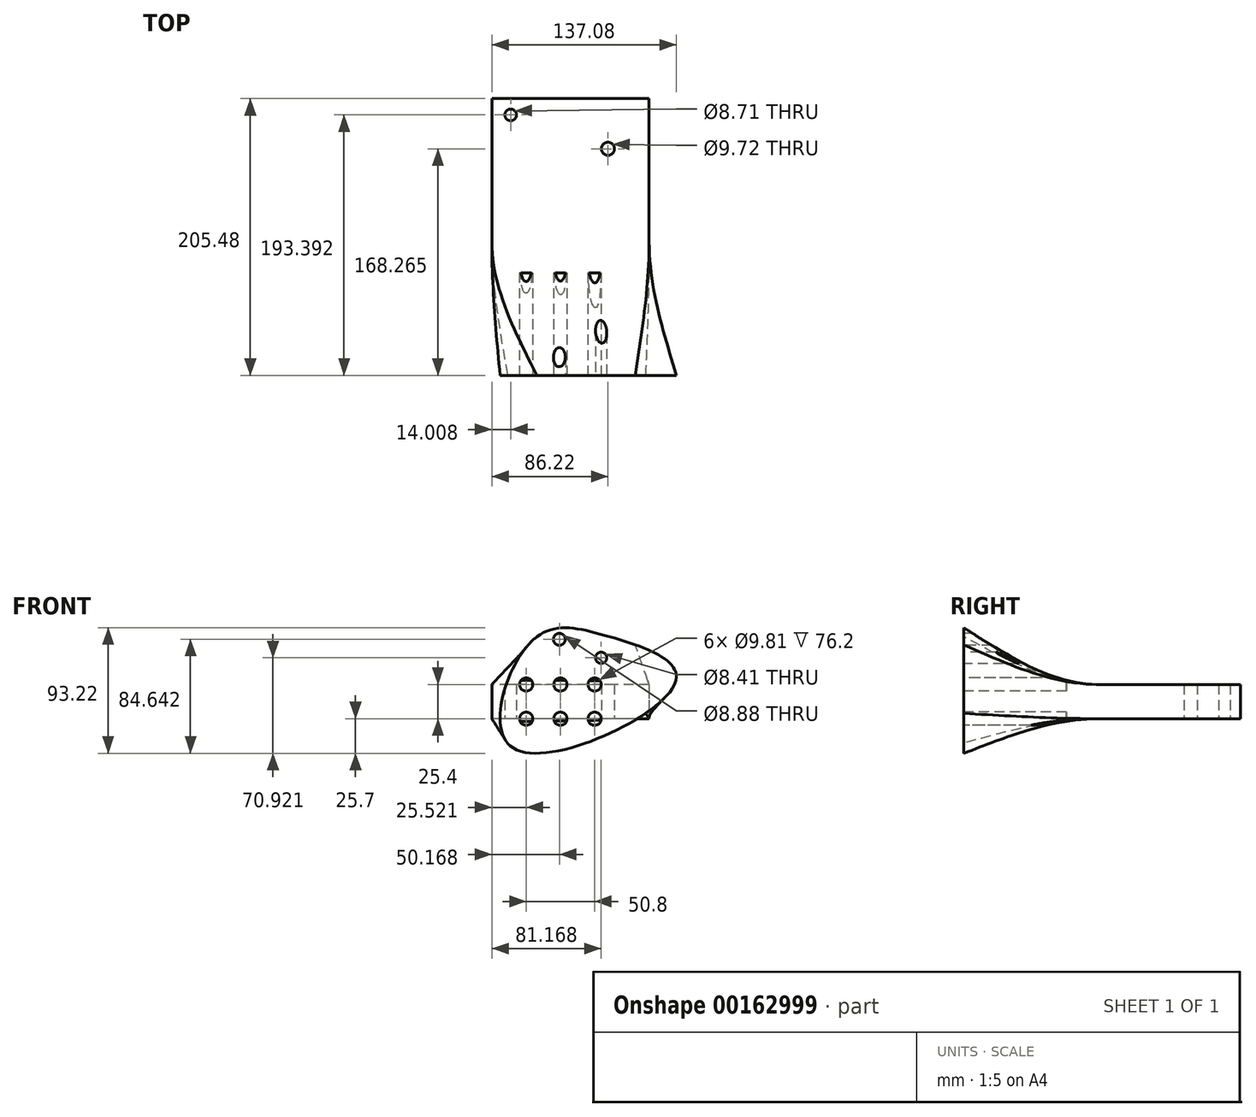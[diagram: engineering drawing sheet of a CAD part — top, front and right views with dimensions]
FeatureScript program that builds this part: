
annotation { "Feature Type Name" : "Feature", "Feature Type Description" : "" }
export const myFeature = defineFeature(function(context is Context, id is Id, definition is map)
    precondition{}
    {
        {
            var Q0;
            Q0=qCreatedBy(makeId("Top.planeOp"),FACE);
            var sketch = newSketch(context, id + "F0", { "sketchPlane" : qUnion([Q0])});
            skLineSegment(sketch, "E0.bottom", {"start": v(58.4, 53.08) * mm, "end": v(-58.4, 53.08) * mm});
            skLineSegment(sketch, "E0.top", {"start": v(58.4, -53.08) * mm, "end": v(-58.4, -53.08) * mm});
            skLineSegment(sketch, "E0.left", {"start": v(58.4, 53.08) * mm, "end": v(58.4, -53.08) * mm});
            skLineSegment(sketch, "E0.right", {"start": v(-58.4, 53.08) * mm, "end": v(-58.4, -53.08) * mm});
            skPoint(sketch, "E0.middle", {"position": v(0, 0) * mm});
            skCircle(sketch, "E1", {"center": v(-44.4, 41) * mm, "radius": 4.35 * mm});
            skCircle(sketch, "E2", {"center": v(27.82, 15.87) * mm, "radius": 4.86 * mm});
            skSolve(sketch);
        }
        {
            var Q0;
            Q0=makeQuery(id+"F0.imprint","IMPRINT",FACE,{"disambiguationData":[TD([[makeQuery(id+"F0.imprint","IMPRINT",EDGE,{"derivedFrom":sQuery(id+"F0.wireOp",EDGE,"E0.bottom")}),1.0]])]});
            extrude(context, id + "F1", {"entities" : qUnion([Q0]), "depth" : 25.4 * mm});
        }
        {
            var Q0;
            Q0=qCreatedBy(makeId("Front.planeOp"),FACE);
            cPlane(context, id + "F2", {"entities" : qUnion([Q0]), "cplaneType" : CPlaneType.OFFSET, "offset" : 152.4 * mm, "width" : 152.4 * mm, "height" : 152.4 * mm});
        }
        {
            var Q0;
            Q0=qCreatedBy(id+"F2.planeOp",FACE);
            var sketch = newSketch(context, id + "F3", { "sketchPlane" : qUnion([Q0])});
            skFitSpline(sketch, "E3", {"points": [v(-29.88, 56.48) * mm, v(26.94, 61.46) * mm, v(78.1, 27.5) * mm, v(-42.1, -22.07) * mm, v(-29.88, 56.48) * mm]});
            skSolve(sketch);
        }
        {
            var Q1;
            Q1=makeQuery(id+"F1.opExtrude","SWEPT_FACE",FACE,{"disambiguationData":[OSD([sQuery(id+"F0.wireOp",EDGE,"E0.top")])]});
            var Q2;
            Q2=makeQuery(id+"F3.imprint","IMPRINT",FACE,{"disambiguationData":[TD([[makeQuery(id+"F3.imprint","IMPRINT",EDGE,{"derivedFrom":sQuery(id+"F3.wireOp",EDGE,"E3")}),-1.0]])]});
            loft(context, id + "F4", {"operationType" : NewBodyOperationType.ADD, "startCondition" : LoftEndDerivativeType.NORMAL_TO_PROFILE, "startMagnitude" : 1, "sheetProfilesArray" : [{ "sheetProfileEntities" : qUnion([Q1]) }, { "sheetProfileEntities" : qUnion([Q2]) }]});
        }
        {
            var Q0;
            Q0=makeQuery(id+"F4.opLoft","CAP_FACE",FACE,{"disambiguationData":[OSD([makeQuery(id+"F3.imprint","IMPRINT",FACE,{"disambiguationData":[TD([[makeQuery(id+"F3.imprint","IMPRINT",EDGE,{"derivedFrom":sQuery(id+"F3.wireOp",EDGE,"E3")}),-1.0]])]})])],"isStart":true});
            var sketch = newSketch(context, id + "F5", { "sketchPlane" : qUnion([Q0])});
            skCircle(sketch, "E4", {"center": v(-8.23, 58.94) * mm, "radius": 4.44 * mm});
            skCircle(sketch, "E5", {"center": v(22.77, 45.22) * mm, "radius": 4.2 * mm});
            skCircle(sketch, "E6", {"center": v(-32.88, 0) * mm, "radius": 4.9 * mm});
            skCircle(sketch, "E7.0.1.0", {"center": v(-32.88, 25.4) * mm, "radius": 4.9 * mm});
            skCircle(sketch, "E7.1.0.0", {"center": v(-7.48, 0) * mm, "radius": 4.9 * mm});
            skCircle(sketch, "E7.1.1.0", {"center": v(-7.48, 25.4) * mm, "radius": 4.9 * mm});
            skCircle(sketch, "E7.2.0.0", {"center": v(17.92, 0) * mm, "radius": 4.9 * mm});
            skCircle(sketch, "E7.2.1.0", {"center": v(17.92, 25.4) * mm, "radius": 4.9 * mm});
            skLineSegment(sketch, "E7.direction1", {"start": v(-32.88, 0) * mm, "end": v(-7.48, 0) * mm, "construction": true});
            skLineSegment(sketch, "E7.direction2", {"start": v(-32.88, 0) * mm, "end": v(-32.88, 25.4) * mm, "construction": true});
            skSolve(sketch);
        }
        {
            var Q0;
            Q0 = qSketchRegion(id + "F5", true);
            extrude(context, id + "F6", {"entities" : qUnion([Q0]), "operationType" : NewBodyOperationType.REMOVE, "oppositeDirection" : true, "depth" : 76.2 * mm});
        }
    });
